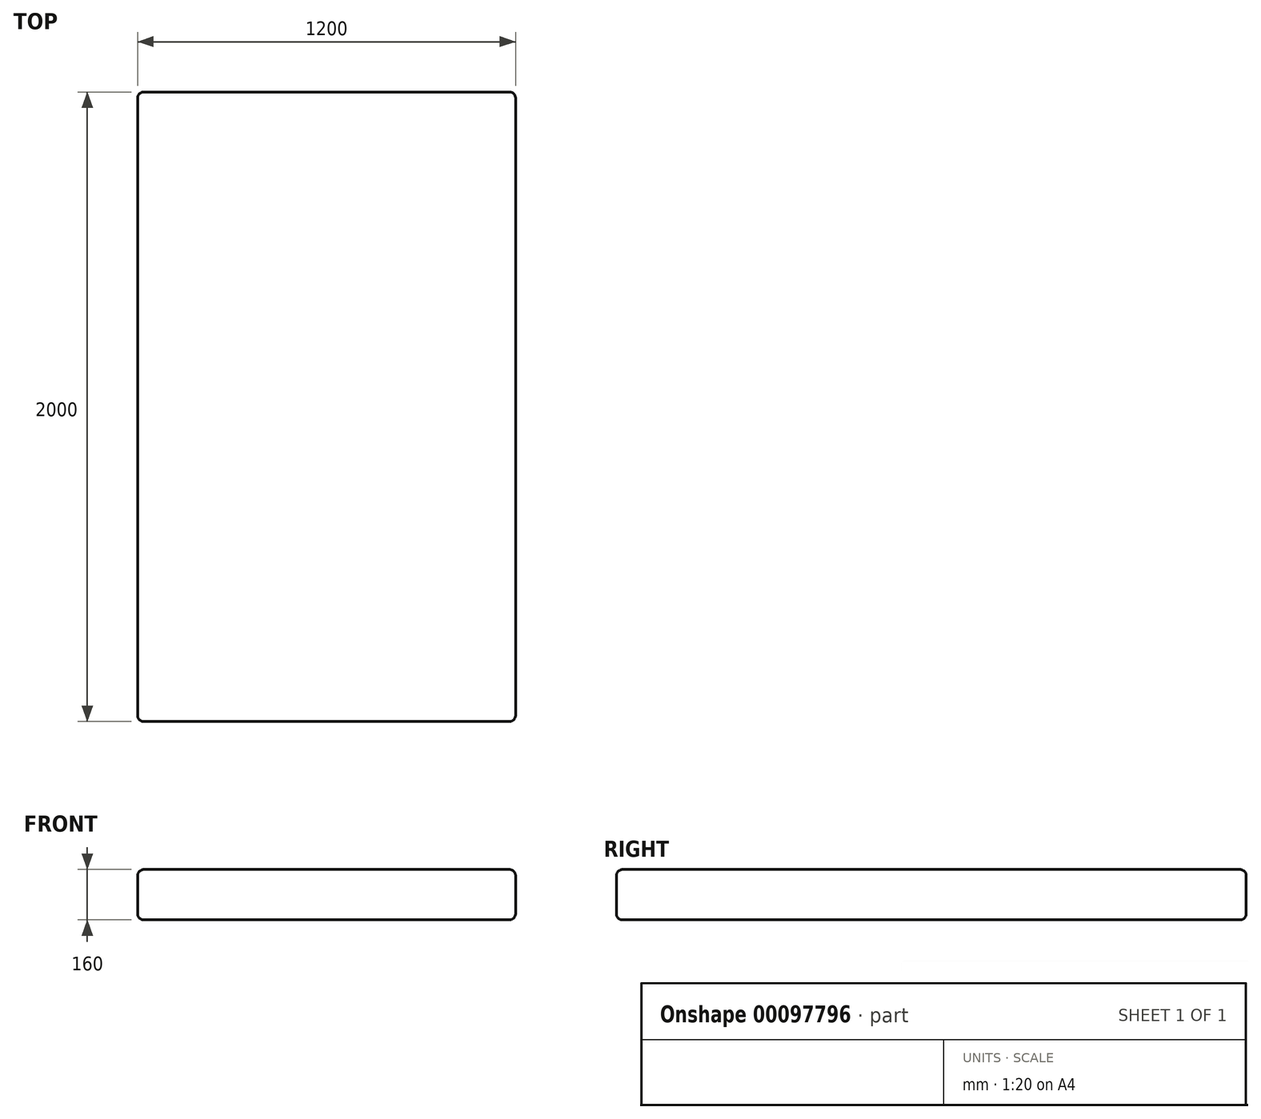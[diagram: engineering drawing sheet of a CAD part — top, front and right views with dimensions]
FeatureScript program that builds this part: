
annotation { "Feature Type Name" : "Feature", "Feature Type Description" : "" }
export const myFeature = defineFeature(function(context is Context, id is Id, definition is map)
    precondition{}
    {
        {
            var Q0;
            Q0=qCreatedBy(makeId("Front.planeOp"),FACE);
            var sketch = newSketch(context, id + "F0", { "sketchPlane" : qUnion([Q0])});
            skLineSegment(sketch, "E0.bottom", {"start": v(0, 0) * mm, "end": v(1200, 0) * mm});
            skLineSegment(sketch, "E0.top", {"start": v(0, 160) * mm, "end": v(1200, 160) * mm});
            skLineSegment(sketch, "E0.left", {"start": v(0, 0) * mm, "end": v(0, 160) * mm});
            skLineSegment(sketch, "E0.right", {"start": v(1200, 0) * mm, "end": v(1200, 160) * mm});
            skSolve(sketch);
        }
        {
            var Q0;
            Q0 = qSketchRegion(id + "F0", true);
            extrude(context, id + "F1", {"entities" : qUnion([Q0]), "oppositeDirection" : true, "depth" : 2000 * mm});
        }
        {
            var Q0;
            Q0=makeQuery(id+"F1.opExtrude","SWEPT_FACE",FACE,{"disambiguationData":[OSD([sQuery(id+"F0.wireOp",EDGE,"E0.top")])]});
            var Q1;
            Q1=makeQuery(id+"F1.opExtrude","SWEPT_FACE",FACE,{"disambiguationData":[OSD([sQuery(id+"F0.wireOp",EDGE,"E0.bottom")])]});
            var Q2;
            Q2=makeQuery(id+"F1.opExtrude","SWEPT_FACE",FACE,{"disambiguationData":[OSD([sQuery(id+"F0.wireOp",EDGE,"E0.right")])]});
            var Q3;
            Q3=makeQuery(id+"F1.opExtrude","SWEPT_FACE",FACE,{"disambiguationData":[OSD([sQuery(id+"F0.wireOp",EDGE,"E0.left")])]});
            fillet(context, id + "F2", {"entities" : qUnion([Q0, Q1, Q2, Q3]), "radius" : 20 * mm, "tangentPropagation" : true, "allowEdgeOverflow" : false});
        }
    });
